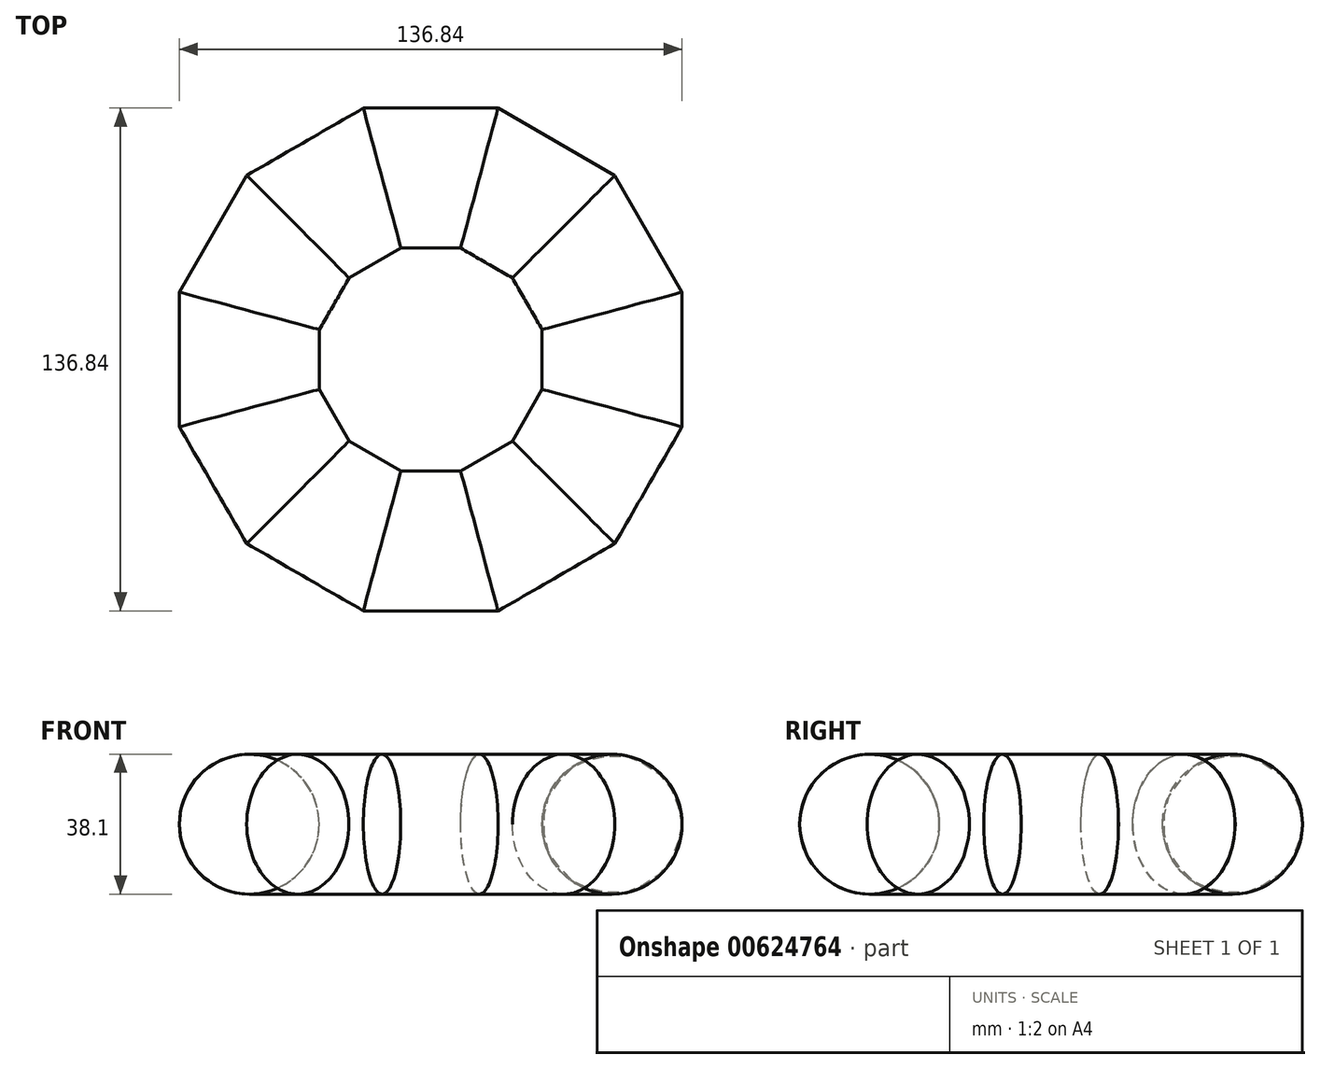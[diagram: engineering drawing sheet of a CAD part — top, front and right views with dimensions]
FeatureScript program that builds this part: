
annotation { "Feature Type Name" : "Feature", "Feature Type Description" : "" }
export const myFeature = defineFeature(function(context is Context, id is Id, definition is map)
    precondition{}
    {
        {
            var Q0;
            Q0=qCreatedBy(makeId("Front.planeOp"),FACE);
            var sketch = newSketch(context, id + "F0", { "sketchPlane" : qUnion([Q0])});
            skCircle(sketch, "E0", {"center": v(-49.37, 0) * mm, "radius": 19.05 * mm});
            skSolve(sketch);
        }
        {
            var Q0;
            Q0=qCreatedBy(makeId("Top.planeOp"),FACE);
            var sketch = newSketch(context, id + "F1", { "sketchPlane" : qUnion([Q0])});
            skLineSegment(sketch, "E1", {"start": v(0, 0) * mm, "end": v(-91.37, 24.48) * mm});
            skLineSegment(sketch, "E2", {"start": v(0, 0) * mm, "end": v(-91.8, -24.6) * mm});
            skSolve(sketch);
        }
        {
            var Q0;
            Q0=sQuery(id+"F1.wireOp",EDGE,"E1");
            var Q1;
            Q1=qCreatedBy(makeId("Top.planeOp"),FACE);
            cPlane(context, id + "F2", {"entities" : qUnion([Q0, Q1]), "cplaneType" : CPlaneType.LINE_ANGLE, "offset" : 25.4 * mm, "angle" : 90 * degree, "width" : 152.4 * mm, "height" : 152.4 * mm});
        }
        {
            var Q0;
            Q0=sQuery(id+"F1.wireOp",EDGE,"E2");
            var Q1;
            Q1=qCreatedBy(makeId("Top.planeOp"),FACE);
            cPlane(context, id + "F3", {"entities" : qUnion([Q0, Q1]), "cplaneType" : CPlaneType.LINE_ANGLE, "offset" : 25.4 * mm, "angle" : 90 * degree, "width" : 152.4 * mm, "height" : 152.4 * mm});
        }
        {
            var Q0;
            Q0=makeQuery(id+"F0.imprint","IMPRINT",FACE,{"disambiguationData":[TD([[makeQuery(id+"F0.imprint","IMPRINT",EDGE,{"derivedFrom":sQuery(id+"F0.wireOp",EDGE,"E0")}),1.0]])]});
            var Q1;
            Q1=qCreatedBy(id+"F2.planeOp",FACE);
            var Q2;
            Q2=qCreatedBy(id+"F3.planeOp",FACE);
            extrude(context, id + "F4", {"entities" : qUnion([Q0]), "endBound" : BoundingType.UP_TO_SURFACE, "oppositeDirection" : true, "depth" : 25.4 * mm, "endBoundEntityFace" : qUnion([Q1]), "offsetDistance" : 25.4 * mm, "hasSecondDirection" : true, "secondDirectionBound" : SecondDirectionBoundingType.UP_TO_SURFACE, "secondDirectionOppositeDirection" : false, "secondDirectionDepth" : 25.4 * mm, "secondDirectionBoundEntityFace" : qUnion([Q2])});
        }
        {
            var Q0;
            Q0=qCreatedBy(makeId("Front.planeOp"),FACE);
            var sketch = newSketch(context, id + "F5", { "sketchPlane" : qUnion([Q0])});
            skLineSegment(sketch, "E3", {"start": v(0, 0) * mm, "end": v(0, 69.63) * mm});
            skSolve(sketch);
        }
        {
            var Q0;
            Q0=makeQuery(id+"F4.opExtrude","SWEPT_BODY",BODY,{"disambiguationData":[OSD([sQuery(id+"F0.wireOp",EDGE,"E0")])]});
            var Q1;
            Q1=sQuery(id+"F5.wireOp",EDGE,"E3");
            circularPattern(context, id + "F6", {"entities" : qUnion([Q0]), "axis" : qUnion([Q1]), "angle" : 360 * degree, "instanceCount" : 12, "equalSpace" : true});
        }
    });
